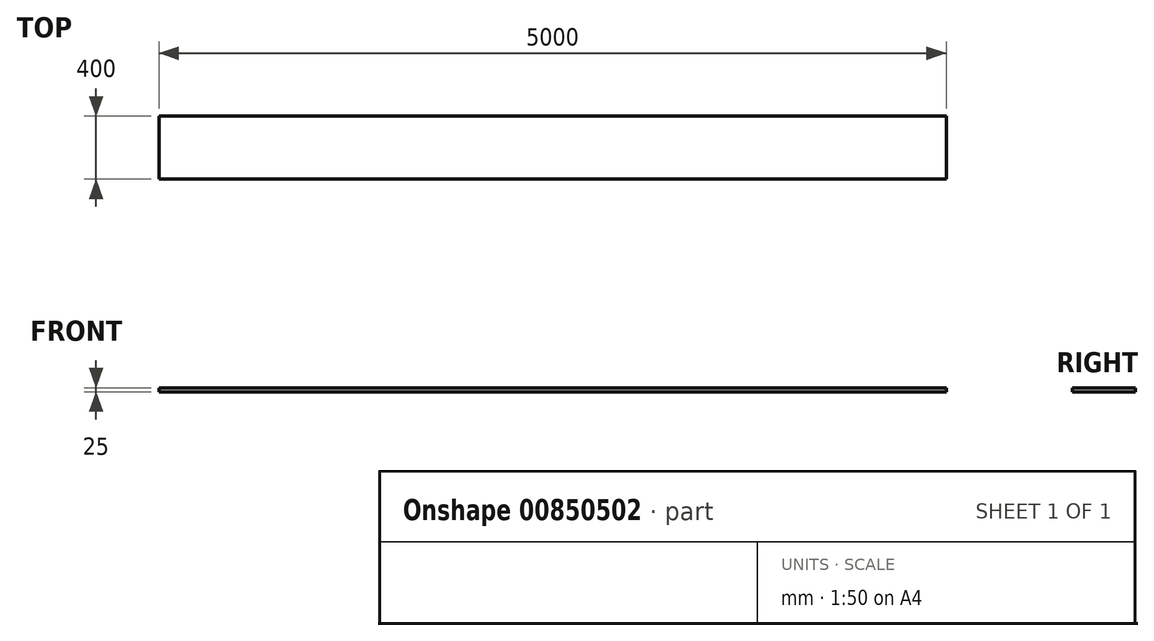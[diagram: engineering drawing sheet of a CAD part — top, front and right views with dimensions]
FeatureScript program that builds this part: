
annotation { "Feature Type Name" : "Feature", "Feature Type Description" : "" }
export const myFeature = defineFeature(function(context is Context, id is Id, definition is map)
    precondition{}
    {
        {
            var Q0;
            Q0=qCreatedBy(makeId("Top.planeOp"),FACE);
            var sketch = newSketch(context, id + "F0", { "sketchPlane" : qUnion([Q0])});
            skLineSegment(sketch, "E0.bottom", {"start": v(-325.78, 309.12) * mm, "end": v(4674.22, 309.12) * mm});
            skLineSegment(sketch, "E0.top", {"start": v(-325.78, -90.88) * mm, "end": v(4674.22, -90.88) * mm});
            skLineSegment(sketch, "E0.left", {"start": v(-325.78, 309.12) * mm, "end": v(-325.78, -90.88) * mm});
            skLineSegment(sketch, "E0.right", {"start": v(4674.22, 309.12) * mm, "end": v(4674.22, -90.88) * mm});
            skSolve(sketch);
        }
        {
            var Q0;
            Q0 = qSketchRegion(id + "F0", true);
            extrude(context, id + "F1", {"entities" : qUnion([Q0]), "depth" : 25 * mm, "offsetDistance" : 25 * mm});
        }
    });
